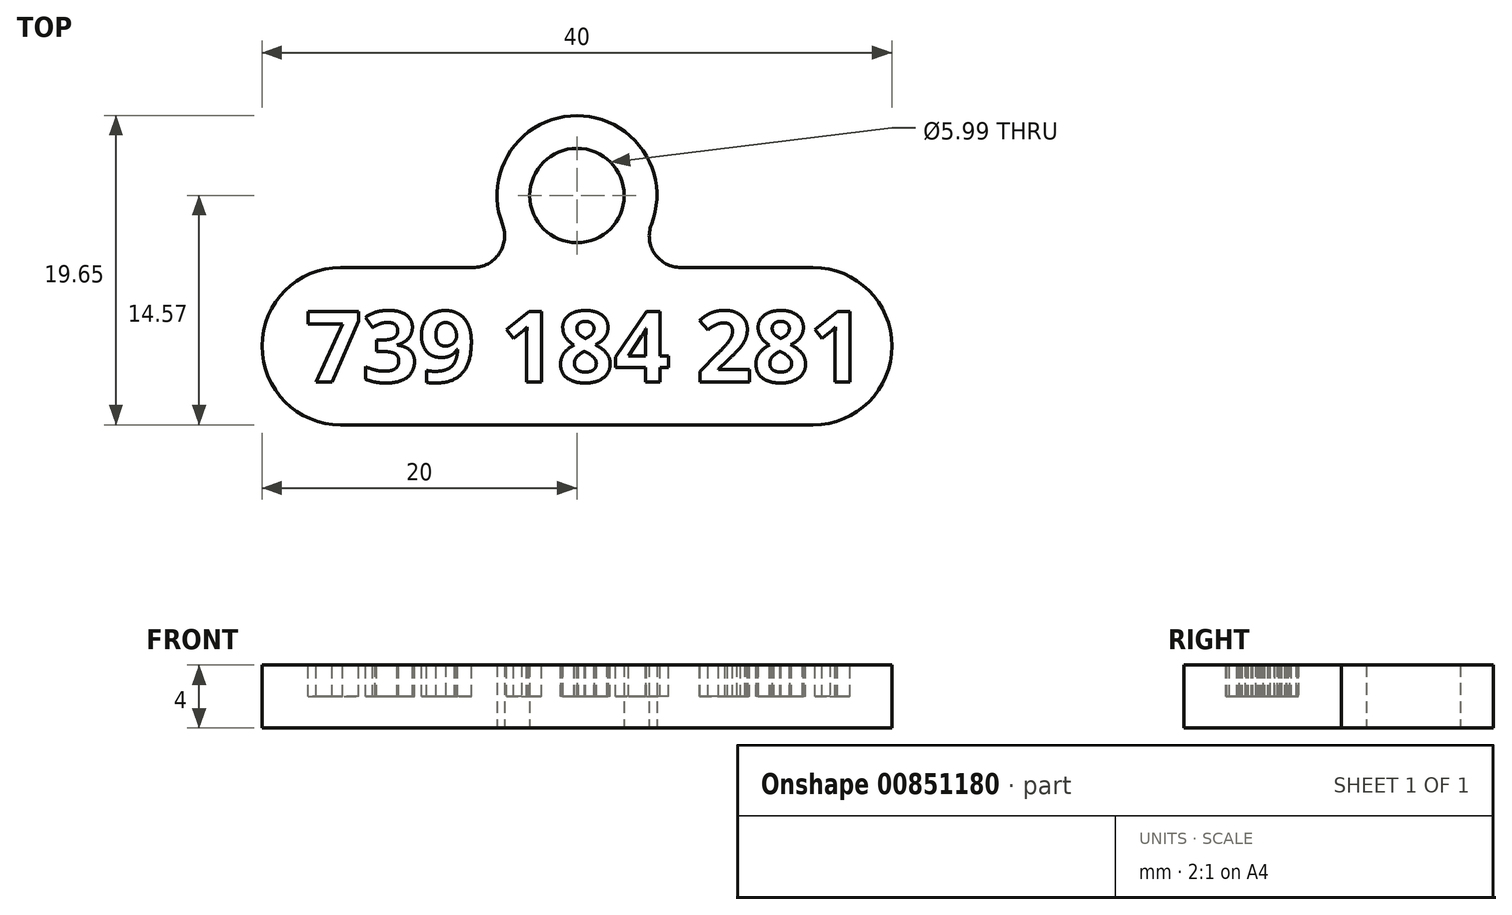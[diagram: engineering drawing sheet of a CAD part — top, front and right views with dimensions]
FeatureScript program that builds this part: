
annotation { "Feature Type Name" : "Feature", "Feature Type Description" : "" }
export const myFeature = defineFeature(function(context is Context, id is Id, definition is map)
    precondition{}
    {
        {
            var Q0;
            Q0=qCreatedBy(makeId("Top.planeOp"),FACE);
            var sketch = newSketch(context, id + "F0", { "sketchPlane" : qUnion([Q0])});
            skLineSegment(sketch, "E0.top", {"start": v(20, -5) * mm, "end": v(-20, -5) * mm});
            skLineSegment(sketch, "E0.left", {"start": v(20, 5) * mm, "end": v(20, -5) * mm});
            skLineSegment(sketch, "E0.right", {"start": v(-20, 5) * mm, "end": v(-20, -5) * mm});
            skPoint(sketch, "E0.middle", {"position": v(0, 0) * mm});
            skCircle(sketch, "E1", {"center": v(0, 9.57) * mm, "radius": 3 * mm});
            skCircle(sketch, "E2", {"center": v(0, 9.57) * mm, "radius": 5.08 * mm});
            skLineSegment(sketch, "E3", {"start": v(-20, 5) * mm, "end": v(-2.2, 5) * mm});
            skLineSegment(sketch, "E4", {"start": v(20, 5) * mm, "end": v(2.2, 5) * mm});
            skSolve(sketch);
        }
        {
            var Q0;
            Q0 = qSketchRegion(id + "F0", true);
            extrude(context, id + "F1", {"entities" : qUnion([Q0]), "depth" : 4 * mm, "offsetDistance" : 25 * mm});
        }
        {
            var Q0;
            Q0=makeQuery(id+"F1.opExtrude","CAP_FACE",FACE,{"disambiguationData":[OSD([sQuery(id+"F0.wireOp",EDGE,"E0.top"),sQuery(id+"F0.wireOp",EDGE,"E0.left"),sQuery(id+"F0.wireOp",EDGE,"E0.right"),sQuery(id+"F0.wireOp",EDGE,"E1"),sQuery(id+"F0.wireOp",EDGE,"E2"),sQuery(id+"F0.wireOp",EDGE,"E3"),sQuery(id+"F0.wireOp",EDGE,"E4")])],"isStart":false});
            var sketch = newSketch(context, id + "F2", { "sketchPlane" : qUnion([Q0])});
            skText(sketch, "E5", { "text": "739 184 281", "fontName": "OpenSans-Bold.ttf"});
            const initialGuessF2  = {"E5": [-0.01726, -0.00228, 1, 0, 0.00453]};
            skSetInitialGuess(sketch, initialGuessF2);
            skSolve(sketch);
        }
        {
            var Q0;
            Q0 = qSketchRegion(id + "F2", true);
            extrude(context, id + "F3", {"entities" : qUnion([Q0]), "operationType" : NewBodyOperationType.REMOVE, "oppositeDirection" : true, "depth" : 2 * mm, "offsetDistance" : 25 * mm});
        }
        {
            var Q0;
            Q0=makeQuery(id+"F1.opExtrude","SWEPT_EDGE",EDGE,{"disambiguationData":[OSD([sQuery(id+"F0.wireOp",EDGE,"E0.top"),sQuery(id+"F0.wireOp",EDGE,"E0.left")])]});
            var Q1;
            Q1=makeQuery(id+"F1.opExtrude","SWEPT_EDGE",EDGE,{"disambiguationData":[OSD([sQuery(id+"F0.wireOp",EDGE,"E0.left"),sQuery(id+"F0.wireOp",EDGE,"E4")])]});
            var Q2;
            Q2=makeQuery(id+"F1.opExtrude","SWEPT_EDGE",EDGE,{"disambiguationData":[OSD([sQuery(id+"F0.wireOp",EDGE,"E0.top"),sQuery(id+"F0.wireOp",EDGE,"E0.right")])]});
            var Q3;
            Q3=makeQuery(id+"F1.opExtrude","SWEPT_EDGE",EDGE,{"disambiguationData":[OSD([sQuery(id+"F0.wireOp",EDGE,"E0.right"),sQuery(id+"F0.wireOp",EDGE,"E3")])]});
            fillet(context, id + "F4", {"entities" : qUnion([Q0, Q1, Q2, Q3]), "radius" : 5 * mm, "tangentPropagation" : true, "allowEdgeOverflow" : false});
        }
        {
            var Q0;
            Q0=makeQuery(id+"F1.opExtrude","SWEPT_EDGE",EDGE,{"disambiguationData":[OSD([sQuery(id+"F0.wireOp",EDGE,"E2"),sQuery(id+"F0.wireOp",EDGE,"E3")])]});
            var Q1;
            Q1=makeQuery(id+"F1.opExtrude","SWEPT_EDGE",EDGE,{"disambiguationData":[OSD([sQuery(id+"F0.wireOp",EDGE,"E2"),sQuery(id+"F0.wireOp",EDGE,"E4")])]});
            fillet(context, id + "F5", {"entities" : qUnion([Q0, Q1]), "radius" : 2 * mm, "tangentPropagation" : true, "allowEdgeOverflow" : false});
        }
    });
